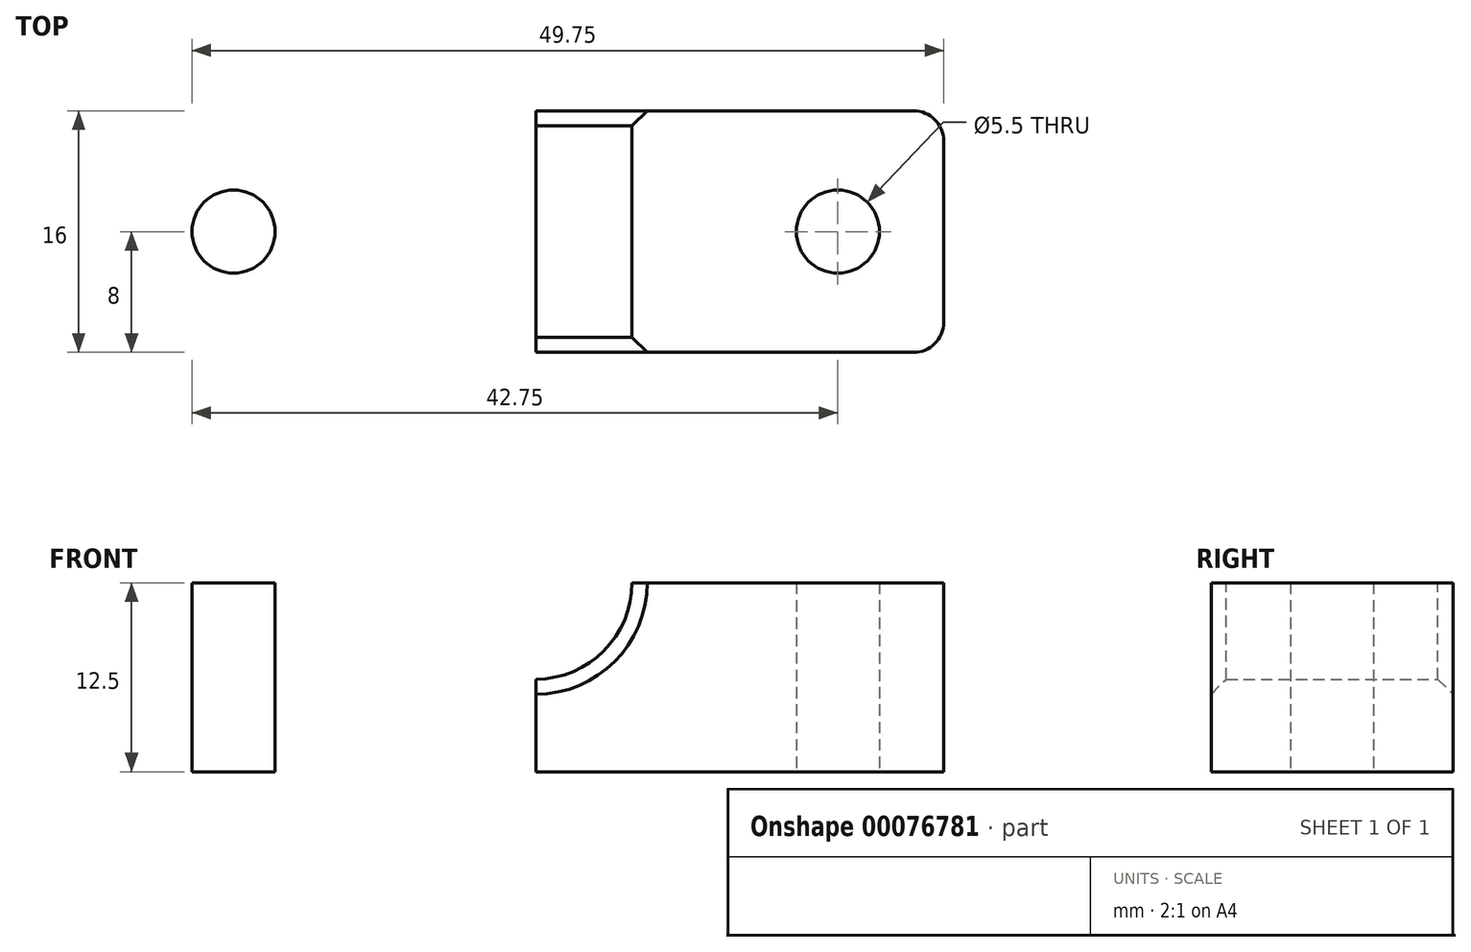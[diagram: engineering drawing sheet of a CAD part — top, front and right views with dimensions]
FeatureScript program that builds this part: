
annotation { "Feature Type Name" : "Feature", "Feature Type Description" : "" }
export const myFeature = defineFeature(function(context is Context, id is Id, definition is map)
    precondition{}
    {
        {
            var Q0;
            Q0=qCreatedBy(makeId("Front.planeOp"),FACE);
            var sketch = newSketch(context, id + "F0", { "sketchPlane" : qUnion([Q0])});
            skLineSegment(sketch, "E0.bottom", {"start": v(-27, 12.5) * mm, "end": v(27, 12.5) * mm});
            skLineSegment(sketch, "E0.top", {"start": v(-27, -12.5) * mm, "end": v(27, -12.5) * mm});
            skLineSegment(sketch, "E0.left", {"start": v(-27, 12.5) * mm, "end": v(-27, -12.5) * mm});
            skLineSegment(sketch, "E0.right", {"start": v(27, 12.5) * mm, "end": v(27, -12.5) * mm});
            skLineSegment(sketch, "E1", {"start": v(-27, 0) * mm, "end": v(27, 0) * mm});
            skPoint(sketch, "E2", {"position": v(0, 0) * mm});
            skCircle(sketch, "E3", {"center": v(0, 0) * mm, "radius": 6.38 * mm});
            skSolve(sketch);
        }
        {
            var Q0;
            {var subQ1=sQuery(id+"F0.wireOp",EDGE,"E0.top");Q0=makeQuery(id+"F0.imprint","IMPRINT",FACE,{"disambiguationData":[TD([[makeQuery(id+"F0.imprint","IMPRINT",EDGE,{"derivedFrom":subQ1}),1.0]])]});}
            extrude(context, id + "F1", {"entities" : qUnion([Q0]), "depth" : 16 * mm});
        }
        {
            var Q0;
            Q0=makeQuery(id+"F1.opExtrude","SWEPT_FACE",FACE,{"disambiguationData":[OSD([sQuery(id+"F0.wireOp",EDGE,"E0.top")])]});
            var sketch = newSketch(context, id + "F2", { "sketchPlane" : qUnion([Q0])});
            skLineSegment(sketch, "E4", {"start": v(0, 0) * mm, "end": v(0, 16) * mm});
            skLineSegment(sketch, "E5", {"start": v(-27, 8) * mm, "end": v(27, 8) * mm});
            skCircle(sketch, "E6", {"center": v(-20, 8) * mm, "radius": 2.75 * mm});
            skCircle(sketch, "E7.MirrorC", {"center": v(20, 8) * mm, "radius": 2.75 * mm});
            skSolve(sketch);
        }
        {
            var Q0;
            {var subQ0=sQuery(id+"F2.wireOp",EDGE,"E6");var subQ1=sQuery(id+"F2.wireOp",EDGE,"E5");var subQ2=makeQuery(id+"F2.imprint","INTERSECT",VERTEX,{"disambiguationData":[OD(0.0)],"derivedFrom":[subQ1,subQ0]});Q0=makeQuery(id+"F2.imprint","IMPRINT",FACE,{"disambiguationData":[TD([[makeQuery(id+"F2.imprint","IMPRINT",EDGE,{"disambiguationData":[TD([[subQ2,-1.0]])],"derivedFrom":subQ1}),1.0]])]});}
            var Q1;
            {var subQ0=sQuery(id+"F2.wireOp",EDGE,"E6");var subQ1=sQuery(id+"F2.wireOp",EDGE,"E5");var subQ2=makeQuery(id+"F2.imprint","INTERSECT",VERTEX,{"disambiguationData":[OD(0.0)],"derivedFrom":[subQ1,subQ0]});Q1=makeQuery(id+"F2.imprint","IMPRINT",FACE,{"disambiguationData":[TD([[makeQuery(id+"F2.imprint","IMPRINT",EDGE,{"disambiguationData":[TD([[subQ2,-1.0]])],"derivedFrom":subQ1}),-1.0]])]});}
            var Q2;
            {var subQ0=sQuery(id+"F2.wireOp",EDGE,"E7.MirrorC");var subQ1=sQuery(id+"F2.wireOp",EDGE,"E5");var subQ2=makeQuery(id+"F2.imprint","INTERSECT",VERTEX,{"disambiguationData":[OD(0.0)],"derivedFrom":[subQ1,subQ0]});Q2=makeQuery(id+"F2.imprint","IMPRINT",FACE,{"disambiguationData":[TD([[makeQuery(id+"F2.imprint","IMPRINT",EDGE,{"disambiguationData":[TD([[subQ2,-1.0]])],"derivedFrom":subQ1}),1.0]])]});}
            var Q3;
            {var subQ0=sQuery(id+"F2.wireOp",EDGE,"E7.MirrorC");var subQ1=sQuery(id+"F2.wireOp",EDGE,"E5");var subQ2=makeQuery(id+"F2.imprint","INTERSECT",VERTEX,{"disambiguationData":[OD(0.0)],"derivedFrom":[subQ1,subQ0]});Q3=makeQuery(id+"F2.imprint","IMPRINT",FACE,{"disambiguationData":[TD([[makeQuery(id+"F2.imprint","IMPRINT",EDGE,{"disambiguationData":[TD([[subQ2,-1.0]])],"derivedFrom":subQ1}),-1.0]])]});}
            extrude(context, id + "F3", {"entities" : qUnion([Q0, Q1, Q2, Q3]), "operationType" : NewBodyOperationType.REMOVE, "endBound" : BoundingType.THROUGH_ALL, "oppositeDirection" : true, "depth" : 25 * mm});
        }
        {
            var Q0;
            Q0=makeQuery(id+"F1.opExtrude","CAP_EDGE",EDGE,{"disambiguationData":[OSD([sQuery(id+"F0.wireOp",EDGE,"E3")])],"isStart":false});
            var Q1;
            Q1=makeQuery(id+"F1.opExtrude","CAP_EDGE",EDGE,{"disambiguationData":[OSD([sQuery(id+"F0.wireOp",EDGE,"E3")])],"isStart":true});
            chamfer(context, id + "F4", {"entities" : qUnion([Q0, Q1]), "width" : 1 * mm, "tangentPropagation" : true});
        }
        {
            var Q0;
            Q0=makeQuery(id+"F1.opExtrude","CAP_EDGE",EDGE,{"disambiguationData":[OSD([sQuery(id+"F0.wireOp",EDGE,"E0.left")])],"isStart":false});
            var Q1;
            Q1=makeQuery(id+"F1.opExtrude","CAP_EDGE",EDGE,{"disambiguationData":[OSD([sQuery(id+"F0.wireOp",EDGE,"E0.right")])],"isStart":false});
            var Q2;
            Q2=makeQuery(id+"F1.opExtrude","CAP_EDGE",EDGE,{"disambiguationData":[OSD([sQuery(id+"F0.wireOp",EDGE,"E0.right")])],"isStart":true});
            var Q3;
            Q3=makeQuery(id+"F1.opExtrude","CAP_EDGE",EDGE,{"disambiguationData":[OSD([sQuery(id+"F0.wireOp",EDGE,"E0.left")])],"isStart":true});
            fillet(context, id + "F5", {"entities" : qUnion([Q0, Q1, Q2, Q3]), "radius" : 2 * mm, "tangentPropagation" : true, "allowEdgeOverflow" : false});
        }
    });
